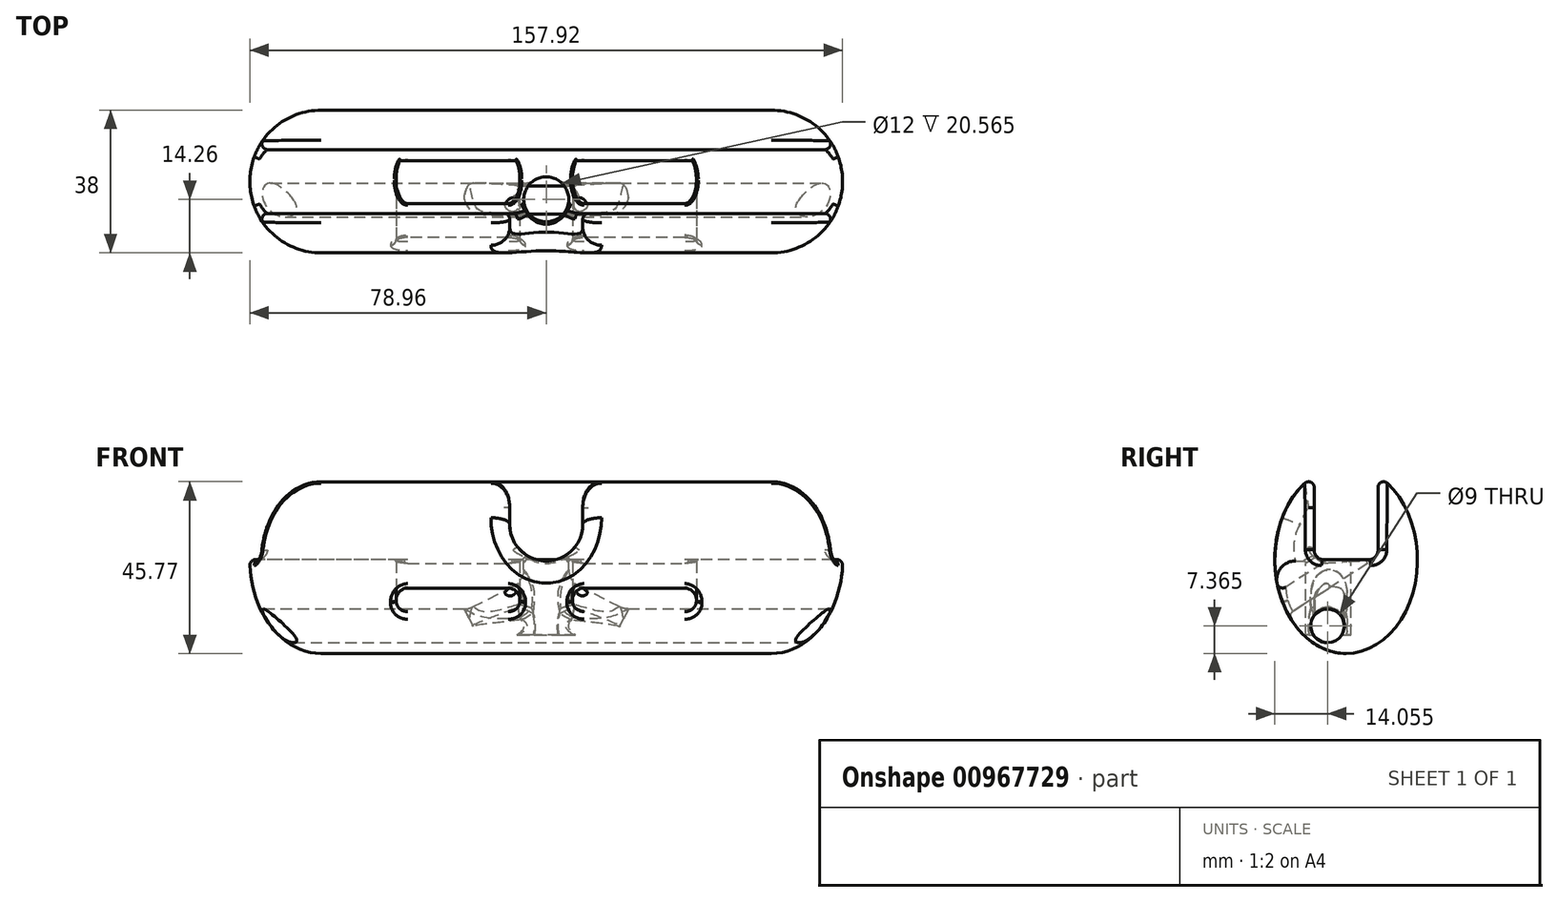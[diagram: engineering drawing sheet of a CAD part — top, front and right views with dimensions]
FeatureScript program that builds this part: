
annotation { "Feature Type Name" : "Feature", "Feature Type Description" : "" }
export const myFeature = defineFeature(function(context is Context, id is Id, definition is map)
    precondition{}
    {
        {
            var Q0;
            Q0=qCreatedBy(makeId("Right.planeOp"),FACE);
            var sketch = newSketch(context, id + "F0", { "sketchPlane" : qUnion([Q0])});
            skEllipse(sketch, "E0", {"center": v(0, 0) * mm, "majorRadius": 25 * mm, "minorRadius": 19 * mm, "majorAxis": v(0, -1)});
            skSolve(sketch);
        }
        {
            var Q0;
            Q0 = qSketchRegion(id + "F0", true);
            extrude(context, id + "F1", {"entities" : qUnion([Q0]), "depth" : 120 * mm, "offsetDistance" : 25 * mm, "symmetric" : true});
        }
        {
            var Q0;
            Q0=makeQuery(id+"F1.opExtrude","CAP_FACE",FACE,{"disambiguationData":[OSD([sQuery(id+"F0.wireOp",EDGE,"E0")])],"isStart":false});
            var sketch = newSketch(context, id + "F2", { "sketchPlane" : qUnion([Q0])});
            skEllipticalArc(sketch, "E1", {});
            skLineSegment(sketch, "E2", {"start": v(0, 25) * mm, "end": v(0, -25) * mm});
            const initialGuessF2  = {"E1": [0, 0, 0, -1, 0.025, 0.019, 3.141592653589793, 0]};
            skSetInitialGuess(sketch, initialGuessF2);
            skSolve(sketch);
        }
        {
            var Q0;
            Q0=makeQuery(id+"F2.imprint","IMPRINT",FACE,{"disambiguationData":[TD([[makeQuery(id+"F2.imprint","IMPRINT",EDGE,{"derivedFrom":sQuery(id+"F2.wireOp",EDGE,"E1")}),1.0]])]});
            var Q1;
            Q1=sQuery(id+"F2.wireOp",EDGE,"E2");
            revolve(context, id + "F3", {"operationType" : NewBodyOperationType.ADD, "surfaceOperationType" : NewSurfaceOperationType.NEW, "entities" : qUnion([Q0]), "axis" : qUnion([Q1]), "revolveType" : RevolveType.FULL});
        }
        {
            var Q0;
            Q0=makeQuery(id+"F1.opExtrude","CAP_FACE",FACE,{"disambiguationData":[OSD([sQuery(id+"F0.wireOp",EDGE,"E0")])],"isStart":true});
            var sketch = newSketch(context, id + "F4", { "sketchPlane" : qUnion([Q0])});
            skEllipticalArc(sketch, "E3", {});
            skLineSegment(sketch, "E4", {"start": v(0, 25) * mm, "end": v(0, -25) * mm});
            const initialGuessF4  = {"E3": [0, 0, 0, -1, 0.025, 0.019, 3.141592653589793, 0]};
            skSetInitialGuess(sketch, initialGuessF4);
            skSolve(sketch);
        }
        {
            var Q0;
            Q0=makeQuery(id+"F4.imprint","IMPRINT",FACE,{"disambiguationData":[TD([[makeQuery(id+"F4.imprint","IMPRINT",EDGE,{"derivedFrom":sQuery(id+"F4.wireOp",EDGE,"E3")}),-1.0]])]});
            var Q1;
            Q1=sQuery(id+"F4.wireOp",EDGE,"E4");
            revolve(context, id + "F5", {"operationType" : NewBodyOperationType.ADD, "surfaceOperationType" : NewSurfaceOperationType.NEW, "entities" : qUnion([Q0]), "axis" : qUnion([Q1]), "revolveType" : RevolveType.FULL});
        }
        {
            var Q0;
            Q0=qCreatedBy(makeId("Right.planeOp"),FACE);
            var sketch = newSketch(context, id + "F6", { "sketchPlane" : qUnion([Q0])});
            skCircle(sketch, "E5", {"center": v(-4.95, -17.63) * mm, "radius": 4.5 * mm});
            skSolve(sketch);
        }
        {
            var Q0;
            Q0 = qSketchRegion(id + "F6", true);
            extrude(context, id + "F7", {"entities" : qUnion([Q0]), "operationType" : NewBodyOperationType.REMOVE, "oppositeDirection" : true, "depth" : 158.8 * mm, "offsetDistance" : 25 * mm, "symmetric" : true});
        }
        {
            var Q0;
            Q0=qCreatedBy(makeId("Top.planeOp"),FACE);
            cPlane(context, id + "F8", {"entities" : qUnion([Q0]), "cplaneType" : CPlaneType.OFFSET, "offset" : 25 * mm, "width" : 150 * mm, "height" : 150 * mm});
        }
        {
            var Q0;
            Q0=qCreatedBy(id+"F8.planeOp",FACE);
            var sketch = newSketch(context, id + "F9", { "sketchPlane" : qUnion([Q0])});
            skLineSegment(sketch, "E6.bottom", {"start": v(79.5, -8.5) * mm, "end": v(-79.5, -8.5) * mm});
            skLineSegment(sketch, "E6.top", {"start": v(79.5, 8.5) * mm, "end": v(-79.5, 8.5) * mm});
            skLineSegment(sketch, "E6.left", {"start": v(79.5, -8.5) * mm, "end": v(79.5, 8.5) * mm});
            skLineSegment(sketch, "E6.right", {"start": v(-79.5, -8.5) * mm, "end": v(-79.5, 8.5) * mm});
            skPoint(sketch, "E6.middle", {"position": v(0, 0) * mm});
            skSolve(sketch);
        }
        {
            var Q0;
            Q0 = qSketchRegion(id + "F9", true);
            extrude(context, id + "F10", {"entities" : qUnion([Q0]), "operationType" : NewBodyOperationType.REMOVE, "oppositeDirection" : true, "depth" : 25 * mm, "offsetDistance" : 25 * mm});
        }
        {
            var Q0;
            Q0=qCreatedBy(makeId("Front.planeOp"),FACE);
            cPlane(context, id + "F11", {"entities" : qUnion([Q0]), "cplaneType" : CPlaneType.OFFSET, "offset" : 5.2 * mm, "width" : 150 * mm, "height" : 150 * mm});
        }
        {
            var Q0;
            Q0=qCreatedBy(id+"F11.planeOp",FACE);
            var sketch = newSketch(context, id + "F12", { "sketchPlane" : qUnion([Q0])});
            skArc(sketch, "E7", {"start": v(-9.74, 9.4) * mm, "mid": v(0, -0.34) * mm, "end": v(9.74, 9.4) * mm});
            skLineSegment(sketch, "E8", {"start": v(-9.74, 9.4) * mm, "end": v(-9.74, 24.15) * mm});
            skLineSegment(sketch, "E9", {"start": v(9.74, 9.4) * mm, "end": v(9.74, 24.15) * mm});
            skLineSegment(sketch, "E10", {"start": v(9.74, 24.15) * mm, "end": v(-9.74, 24.15) * mm});
            skSolve(sketch);
        }
        {
            var Q0;
            Q0 = qSketchRegion(id + "F12", true);
            extrude(context, id + "F13", {"entities" : qUnion([Q0]), "operationType" : NewBodyOperationType.REMOVE, "depth" : 27.5 * mm, "offsetDistance" : 25 * mm});
        }
        {
            var Q0;
            Q0=makeQuery(id+"F13.boolean.opBoolean","INTERSECT",EDGE,{"derivedFrom":[makeQuery(id+"F1.opExtrude","SWEPT_FACE",FACE,{"disambiguationData":[OSD([sQuery(id+"F0.wireOp",EDGE,"E0")])]}),makeQuery(id+"F13.opExtrude","SWEPT_FACE",FACE,{"disambiguationData":[OSD([sQuery(id+"F12.wireOp",EDGE,"E7")])]})]});
            var Q1;
            Q1=makeQuery(id+"F13.boolean.opBoolean","INTERSECT",EDGE,{"derivedFrom":[makeQuery(id+"F1.opExtrude","SWEPT_FACE",FACE,{"disambiguationData":[OSD([sQuery(id+"F0.wireOp",EDGE,"E0")])]}),makeQuery(id+"F13.opExtrude","SWEPT_FACE",FACE,{"disambiguationData":[OSD([sQuery(id+"F12.wireOp",EDGE,"E9")])]})]});
            var Q2;
            Q2=makeQuery(id+"F13.boolean.opBoolean","INTERSECT",EDGE,{"derivedFrom":[makeQuery(id+"F1.opExtrude","SWEPT_FACE",FACE,{"disambiguationData":[OSD([sQuery(id+"F0.wireOp",EDGE,"E0")])]}),makeQuery(id+"F13.opExtrude","SWEPT_FACE",FACE,{"disambiguationData":[OSD([sQuery(id+"F12.wireOp",EDGE,"E8")])]})]});
            fillet(context, id + "F14", {"entities" : qUnion([Q0, Q1, Q2]), "radius" : 5 * mm, "tangentPropagation" : true, "allowEdgeOverflow" : false});
        }
        {
            var Q0;
            {var subQ0=sQuery(id+"F9.wireOp",EDGE,"E6.bottom");Q0=makeQuery(id+"F13.boolean.opBoolean","SPLIT",EDGE,{"disambiguationData":[TD([makeQuery(id+"F3.opRevolve","SWEPT_FACE",FACE,{"disambiguationData":[OSD([sQuery(id+"F2.wireOp",EDGE,"E1")])]})])],"derivedFrom":makeQuery(id+"F10.boolean.opBoolean","COPY",EDGE,{"derivedFrom":makeQuery(id+"F10.opExtrude","CAP_EDGE",EDGE,{"disambiguationData":[OSD([subQ0])],"isStart":false})})});}
            var Q1;
            {var subQ0=sQuery(id+"F9.wireOp",EDGE,"E6.bottom");Q1=makeQuery(id+"F13.boolean.opBoolean","SPLIT",EDGE,{"disambiguationData":[TD([makeQuery(id+"F5.opRevolve","SWEPT_FACE",FACE,{"disambiguationData":[OSD([sQuery(id+"F4.wireOp",EDGE,"E3")])]})])],"derivedFrom":makeQuery(id+"F10.boolean.opBoolean","COPY",EDGE,{"derivedFrom":makeQuery(id+"F10.opExtrude","CAP_EDGE",EDGE,{"disambiguationData":[OSD([subQ0])],"isStart":false})})});}
            var Q2;
            Q2=makeQuery(id+"F10.boolean.opBoolean","COPY",EDGE,{"derivedFrom":makeQuery(id+"F10.opExtrude","CAP_EDGE",EDGE,{"disambiguationData":[OSD([sQuery(id+"F9.wireOp",EDGE,"E6.top")])],"isStart":false})});
            fillet(context, id + "F15", {"entities" : qUnion([Q0, Q1, Q2]), "radius" : 2.5 * mm, "tangentPropagation" : true, "allowEdgeOverflow" : false});
        }
        {
            var Q0;
            Q0=qCreatedBy(makeId("Top.planeOp"),FACE);
            var sketch = newSketch(context, id + "F16", { "sketchPlane" : qUnion([Q0])});
            skCircle(sketch, "E11", {"center": v(0, -4.74) * mm, "radius": 6 * mm});
            skSolve(sketch);
        }
        {
            var Q0;
            {var subQ0=makeQuery(id+"F1.opExtrude","SWEPT_FACE",FACE,{"disambiguationData":[OSD([sQuery(id+"F0.wireOp",EDGE,"E0")])]});var subQ1=makeQuery(id+"F10.opExtrude","SWEPT_FACE",FACE,{"disambiguationData":[OSD([sQuery(id+"F9.wireOp",EDGE,"E6.bottom")])]});Q0=makeQuery(id+"F13.boolean.opBoolean","SPLIT",EDGE,{"disambiguationData":[TD([makeQuery(id+"F5.opRevolve","SWEPT_FACE",FACE,{"disambiguationData":[OSD([sQuery(id+"F4.wireOp",EDGE,"E3")])]})])],"derivedFrom":makeQuery(id+"F10.boolean.opBoolean","INTERSECT",EDGE,{"derivedFrom":[subQ0,subQ1]})});}
            var Q1;
            {var subQ0=makeQuery(id+"F1.opExtrude","SWEPT_FACE",FACE,{"disambiguationData":[OSD([sQuery(id+"F0.wireOp",EDGE,"E0")])]});var subQ1=makeQuery(id+"F10.opExtrude","SWEPT_FACE",FACE,{"disambiguationData":[OSD([sQuery(id+"F9.wireOp",EDGE,"E6.bottom")])]});Q1=makeQuery(id+"F13.boolean.opBoolean","SPLIT",EDGE,{"disambiguationData":[TD([makeQuery(id+"F3.opRevolve","SWEPT_FACE",FACE,{"disambiguationData":[OSD([sQuery(id+"F2.wireOp",EDGE,"E1")])]})])],"derivedFrom":makeQuery(id+"F10.boolean.opBoolean","INTERSECT",EDGE,{"derivedFrom":[subQ0,subQ1]})});}
            fillet(context, id + "F17", {"entities" : qUnion([Q0, Q1]), "radius" : 1.5 * mm, "tangentPropagation" : true, "allowEdgeOverflow" : false});
        }
        {
            var Q0;
            Q0 = qSketchRegion(id + "F16", true);
            extrude(context, id + "F18", {"entities" : qUnion([Q0]), "operationType" : NewBodyOperationType.REMOVE, "oppositeDirection" : true, "depth" : 40.2 * mm, "offsetDistance" : 25 * mm, "symmetric" : true});
        }
        {
            var Q0;
            Q0=makeQuery(id+"F18.boolean.opBoolean","INTERSECT",EDGE,{"derivedFrom":[makeQuery(id+"F10.boolean.opBoolean","COPY",FACE,{"derivedFrom":makeQuery(id+"F10.opExtrude","CAP_FACE",FACE,{"disambiguationData":[OSD([sQuery(id+"F9.wireOp",EDGE,"E6.bottom"),sQuery(id+"F9.wireOp",EDGE,"E6.top"),sQuery(id+"F9.wireOp",EDGE,"E6.left"),sQuery(id+"F9.wireOp",EDGE,"E6.right")])],"isStart":false})}),makeQuery(id+"F18.opExtrude","SWEPT_FACE",FACE,{"disambiguationData":[OSD([sQuery(id+"F16.wireOp",EDGE,"E11")])]})]});
            var Q1;
            {var subQ0=sQuery(id+"F9.wireOp",EDGE,"E6.bottom");Q1=makeQuery(id+"F18.boolean.opBoolean","INTERSECT",EDGE,{"derivedFrom":[makeQuery(id+"F15.opFillet","BLEND_FACE",FACE,{"disambiguationData":[OSD([subQ0]),TDD([makeQuery(id+"F13.boolean.opBoolean","SPLIT",EDGE,{"disambiguationData":[TD([makeQuery(id+"F3.opRevolve","SWEPT_FACE",FACE,{"disambiguationData":[OSD([sQuery(id+"F2.wireOp",EDGE,"E1")])]})])],"derivedFrom":makeQuery(id+"F10.boolean.opBoolean","COPY",EDGE,{"derivedFrom":makeQuery(id+"F10.opExtrude","CAP_EDGE",EDGE,{"disambiguationData":[OSD([subQ0])],"isStart":false})})})])]}),makeQuery(id+"F18.opExtrude","SWEPT_FACE",FACE,{"disambiguationData":[OSD([sQuery(id+"F16.wireOp",EDGE,"E11")])]})]});}
            var Q2;
            {var subQ0=sQuery(id+"F12.wireOp",EDGE,"E7");var subQ1=makeQuery(id+"F13.opExtrude","SWEPT_FACE",FACE,{"disambiguationData":[OSD([subQ0])]});var subQ2=sQuery(id+"F9.wireOp",EDGE,"E6.bottom");Q2=makeQuery(id+"F18.boolean.opBoolean","INTERSECT",EDGE,{"derivedFrom":[makeQuery(id+"F17.opFillet","BLEND_FACE",FACE,{"disambiguationData":[OSD([subQ2,subQ0]),TDD([makeQuery(id+"F15.opFillet","BLEND_EDGE",EDGE,{"blendedFrom":[makeQuery(id+"F13.boolean.opBoolean","SPLIT",EDGE,{"disambiguationData":[TD([makeQuery(id+"F3.opRevolve","SWEPT_FACE",FACE,{"disambiguationData":[OSD([sQuery(id+"F2.wireOp",EDGE,"E1")])]})])],"derivedFrom":makeQuery(id+"F10.boolean.opBoolean","COPY",EDGE,{"derivedFrom":makeQuery(id+"F10.opExtrude","CAP_EDGE",EDGE,{"disambiguationData":[OSD([subQ2])],"isStart":false})})}),makeQuery(id+"F13.boolean.opBoolean","COPY",FACE,{"derivedFrom":subQ1})],"blendedInto":[makeQuery(id+"F13.boolean.opBoolean","COPY",FACE,{"derivedFrom":subQ1})]})])]}),makeQuery(id+"F18.opExtrude","SWEPT_FACE",FACE,{"disambiguationData":[OSD([sQuery(id+"F16.wireOp",EDGE,"E11")])]})]});}
            var Q3;
            Q3=makeQuery(id+"F18.boolean.opBoolean","INTERSECT",EDGE,{"derivedFrom":[makeQuery(id+"F13.boolean.opBoolean","COPY",FACE,{"derivedFrom":makeQuery(id+"F13.opExtrude","SWEPT_FACE",FACE,{"disambiguationData":[OSD([sQuery(id+"F12.wireOp",EDGE,"E7")])]})}),makeQuery(id+"F18.opExtrude","SWEPT_FACE",FACE,{"disambiguationData":[OSD([sQuery(id+"F16.wireOp",EDGE,"E11")])]})]});
            var Q4;
            {var subQ0=sQuery(id+"F12.wireOp",EDGE,"E7");var subQ1=makeQuery(id+"F13.opExtrude","SWEPT_FACE",FACE,{"disambiguationData":[OSD([subQ0])]});var subQ2=sQuery(id+"F9.wireOp",EDGE,"E6.bottom");Q4=makeQuery(id+"F18.boolean.opBoolean","INTERSECT",EDGE,{"derivedFrom":[makeQuery(id+"F17.opFillet","BLEND_FACE",FACE,{"disambiguationData":[OSD([subQ2,subQ0]),TDD([makeQuery(id+"F15.opFillet","BLEND_EDGE",EDGE,{"blendedFrom":[makeQuery(id+"F13.boolean.opBoolean","SPLIT",EDGE,{"disambiguationData":[TD([makeQuery(id+"F5.opRevolve","SWEPT_FACE",FACE,{"disambiguationData":[OSD([sQuery(id+"F4.wireOp",EDGE,"E3")])]})])],"derivedFrom":makeQuery(id+"F10.boolean.opBoolean","COPY",EDGE,{"derivedFrom":makeQuery(id+"F10.opExtrude","CAP_EDGE",EDGE,{"disambiguationData":[OSD([subQ2])],"isStart":false})})}),makeQuery(id+"F13.boolean.opBoolean","COPY",FACE,{"derivedFrom":subQ1})],"blendedInto":[makeQuery(id+"F13.boolean.opBoolean","COPY",FACE,{"derivedFrom":subQ1})]})])]}),makeQuery(id+"F18.opExtrude","SWEPT_FACE",FACE,{"disambiguationData":[OSD([sQuery(id+"F16.wireOp",EDGE,"E11")])]})]});}
            var Q5;
            {var subQ0=sQuery(id+"F9.wireOp",EDGE,"E6.bottom");Q5=makeQuery(id+"F18.boolean.opBoolean","INTERSECT",EDGE,{"derivedFrom":[makeQuery(id+"F15.opFillet","BLEND_FACE",FACE,{"disambiguationData":[OSD([subQ0]),TDD([makeQuery(id+"F13.boolean.opBoolean","SPLIT",EDGE,{"disambiguationData":[TD([makeQuery(id+"F5.opRevolve","SWEPT_FACE",FACE,{"disambiguationData":[OSD([sQuery(id+"F4.wireOp",EDGE,"E3")])]})])],"derivedFrom":makeQuery(id+"F10.boolean.opBoolean","COPY",EDGE,{"derivedFrom":makeQuery(id+"F10.opExtrude","CAP_EDGE",EDGE,{"disambiguationData":[OSD([subQ0])],"isStart":false})})})])]}),makeQuery(id+"F18.opExtrude","SWEPT_FACE",FACE,{"disambiguationData":[OSD([sQuery(id+"F16.wireOp",EDGE,"E11")])]})]});}
            fillet(context, id + "F19", {"entities" : qUnion([Q0, Q1, Q2, Q3, Q4, Q5]), "radius" : 0.65 * mm, "tangentPropagation" : true, "allowEdgeOverflow" : false});
        }
        {
            var Q0;
            Q0=makeQuery(id+"F18.boolean.opBoolean","INTERSECT",EDGE,{"disambiguationData":[OD(0.0)],"derivedFrom":[makeQuery(id+"F7.boolean.opBoolean","COPY",FACE,{"derivedFrom":makeQuery(id+"F7.opExtrude","SWEPT_FACE",FACE,{"disambiguationData":[OSD([sQuery(id+"F6.wireOp",EDGE,"E5")])]})}),makeQuery(id+"F18.opExtrude","SWEPT_FACE",FACE,{"disambiguationData":[OSD([sQuery(id+"F16.wireOp",EDGE,"E11")])]})]});
            var Q1;
            Q1=makeQuery(id+"F18.boolean.opBoolean","INTERSECT",EDGE,{"disambiguationData":[OD(1.0)],"derivedFrom":[makeQuery(id+"F7.boolean.opBoolean","COPY",FACE,{"derivedFrom":makeQuery(id+"F7.opExtrude","SWEPT_FACE",FACE,{"disambiguationData":[OSD([sQuery(id+"F6.wireOp",EDGE,"E5")])]})}),makeQuery(id+"F18.opExtrude","SWEPT_FACE",FACE,{"disambiguationData":[OSD([sQuery(id+"F16.wireOp",EDGE,"E11")])]})]});
            fillet(context, id + "F20", {"entities" : qUnion([Q0, Q1]), "radius" : 5 * mm, "tangentPropagation" : true, "allowEdgeOverflow" : false});
        }
        {
            var Q0;
            Q0=qCreatedBy(makeId("Right.planeOp"),FACE);
            var sketch = newSketch(context, id + "F21", { "sketchPlane" : qUnion([Q0])});
            skLineSegment(sketch, "E12", {"start": v(-25.32, 0) * mm, "end": v(-6.7, -28.91) * mm, "construction": true});
            skSolve(sketch);
        }
        {
            var Q0;
            Q0=qCreatedBy(id+"F11.planeOp",FACE);
            var Q1;
            Q1=sQuery(id+"F21.wireOp",EDGE,"E12");
            cPlane(context, id + "F22", {"entities" : qUnion([Q0, Q1]), "cplaneType" : CPlaneType.LINE_ANGLE, "offset" : 25 * mm, "angle" : 0 * degree, "width" : 150 * mm, "height" : 150 * mm});
        }
        {
            var Q0;
            Q0=qCreatedBy(id+"F22.planeOp",FACE);
            var sketch = newSketch(context, id + "F23", { "sketchPlane" : qUnion([Q0])});
            skLineSegment(sketch, "E13.bottom", {"start": v(40, 2.55) * mm, "end": v(7, 2.55) * mm});
            skLineSegment(sketch, "E13.top", {"start": v(40, -3.95) * mm, "end": v(7, -3.95) * mm});
            skLineSegment(sketch, "E13.left", {"start": v(40, 2.55) * mm, "end": v(40, -3.95) * mm});
            skLineSegment(sketch, "E13.right", {"start": v(7, 2.55) * mm, "end": v(7, -3.95) * mm});
            skLineSegment(sketch, "E14.bottom", {"start": v(-7, 2.55) * mm, "end": v(-40, 2.55) * mm});
            skLineSegment(sketch, "E14.top", {"start": v(-7, -3.95) * mm, "end": v(-40, -3.95) * mm});
            skLineSegment(sketch, "E14.left", {"start": v(-7, 2.55) * mm, "end": v(-7, -3.95) * mm});
            skLineSegment(sketch, "E14.right", {"start": v(-40, 2.55) * mm, "end": v(-40, -3.95) * mm});
            skSolve(sketch);
        }
        {
            var Q0;
            Q0 = qSketchRegion(id + "F23", true);
            extrude(context, id + "F24", {"entities" : qUnion([Q0]), "operationType" : NewBodyOperationType.REMOVE, "depth" : 25.6 * mm, "offsetDistance" : 25 * mm});
        }
        {
            var Q0;
            Q0=makeQuery(id+"F24.boolean.opBoolean","COPY",EDGE,{"derivedFrom":makeQuery(id+"F24.opExtrude","SWEPT_EDGE",EDGE,{"disambiguationData":[OSD([sQuery(id+"F23.wireOp",EDGE,"E13.bottom"),sQuery(id+"F23.wireOp",EDGE,"E13.left")])]})});
            var Q1;
            Q1=makeQuery(id+"F24.boolean.opBoolean","COPY",EDGE,{"derivedFrom":makeQuery(id+"F24.opExtrude","SWEPT_EDGE",EDGE,{"disambiguationData":[OSD([sQuery(id+"F23.wireOp",EDGE,"E13.bottom"),sQuery(id+"F23.wireOp",EDGE,"E13.right")])]})});
            var Q2;
            Q2=makeQuery(id+"F24.boolean.opBoolean","COPY",EDGE,{"derivedFrom":makeQuery(id+"F24.opExtrude","SWEPT_EDGE",EDGE,{"disambiguationData":[OSD([sQuery(id+"F23.wireOp",EDGE,"E14.bottom"),sQuery(id+"F23.wireOp",EDGE,"E14.right")])]})});
            var Q3;
            Q3=makeQuery(id+"F24.boolean.opBoolean","COPY",EDGE,{"derivedFrom":makeQuery(id+"F24.opExtrude","SWEPT_EDGE",EDGE,{"disambiguationData":[OSD([sQuery(id+"F23.wireOp",EDGE,"E14.bottom"),sQuery(id+"F23.wireOp",EDGE,"E14.left")])]})});
            var Q4;
            Q4=makeQuery(id+"F24.boolean.opBoolean","COPY",EDGE,{"derivedFrom":makeQuery(id+"F24.opExtrude","SWEPT_EDGE",EDGE,{"disambiguationData":[OSD([sQuery(id+"F23.wireOp",EDGE,"E13.top"),sQuery(id+"F23.wireOp",EDGE,"E13.left")])]})});
            var Q5;
            Q5=makeQuery(id+"F24.boolean.opBoolean","COPY",EDGE,{"derivedFrom":makeQuery(id+"F24.opExtrude","SWEPT_EDGE",EDGE,{"disambiguationData":[OSD([sQuery(id+"F23.wireOp",EDGE,"E14.top"),sQuery(id+"F23.wireOp",EDGE,"E14.left")])]})});
            var Q6;
            Q6=makeQuery(id+"F24.boolean.opBoolean","COPY",EDGE,{"derivedFrom":makeQuery(id+"F24.opExtrude","SWEPT_EDGE",EDGE,{"disambiguationData":[OSD([sQuery(id+"F23.wireOp",EDGE,"E14.top"),sQuery(id+"F23.wireOp",EDGE,"E14.right")])]})});
            var Q7;
            Q7=makeQuery(id+"F24.boolean.opBoolean","COPY",EDGE,{"derivedFrom":makeQuery(id+"F24.opExtrude","SWEPT_EDGE",EDGE,{"disambiguationData":[OSD([sQuery(id+"F23.wireOp",EDGE,"E13.top"),sQuery(id+"F23.wireOp",EDGE,"E13.right")])]})});
            fillet(context, id + "F25", {"entities" : qUnion([Q0, Q1, Q2, Q3, Q4, Q5, Q6, Q7]), "radius" : 3.14 * mm, "tangentPropagation" : true, "allowEdgeOverflow" : false});
        }
        {
            var Q0;
            Q0=makeQuery(id+"F24.boolean.opBoolean","INTERSECT",EDGE,{"derivedFrom":[makeQuery(id+"F1.opExtrude","SWEPT_FACE",FACE,{"disambiguationData":[OSD([sQuery(id+"F0.wireOp",EDGE,"E0")])]}),makeQuery(id+"F24.opExtrude","SWEPT_FACE",FACE,{"disambiguationData":[OSD([sQuery(id+"F23.wireOp",EDGE,"E13.bottom")])]})]});
            var Q1;
            Q1=makeQuery(id+"F25.opFillet","BLEND_EDGE",EDGE,{"blendedFrom":[makeQuery(id+"F24.boolean.opBoolean","COPY",EDGE,{"derivedFrom":makeQuery(id+"F24.opExtrude","SWEPT_EDGE",EDGE,{"disambiguationData":[OSD([sQuery(id+"F23.wireOp",EDGE,"E13.bottom"),sQuery(id+"F23.wireOp",EDGE,"E13.left")])]})}),makeQuery(id+"F1.opExtrude","SWEPT_FACE",FACE,{"disambiguationData":[OSD([sQuery(id+"F0.wireOp",EDGE,"E0")])]})],"blendedInto":[makeQuery(id+"F1.opExtrude","SWEPT_FACE",FACE,{"disambiguationData":[OSD([sQuery(id+"F0.wireOp",EDGE,"E0")])]})]});
            var Q2;
            Q2=makeQuery(id+"F25.opFillet","BLEND_EDGE",EDGE,{"blendedFrom":[makeQuery(id+"F24.boolean.opBoolean","COPY",EDGE,{"derivedFrom":makeQuery(id+"F24.opExtrude","SWEPT_EDGE",EDGE,{"disambiguationData":[OSD([sQuery(id+"F23.wireOp",EDGE,"E13.top"),sQuery(id+"F23.wireOp",EDGE,"E13.left")])]})}),makeQuery(id+"F1.opExtrude","SWEPT_FACE",FACE,{"disambiguationData":[OSD([sQuery(id+"F0.wireOp",EDGE,"E0")])]})],"blendedInto":[makeQuery(id+"F1.opExtrude","SWEPT_FACE",FACE,{"disambiguationData":[OSD([sQuery(id+"F0.wireOp",EDGE,"E0")])]})]});
            var Q3;
            Q3=makeQuery(id+"F24.boolean.opBoolean","INTERSECT",EDGE,{"derivedFrom":[makeQuery(id+"F1.opExtrude","SWEPT_FACE",FACE,{"disambiguationData":[OSD([sQuery(id+"F0.wireOp",EDGE,"E0")])]}),makeQuery(id+"F24.opExtrude","SWEPT_FACE",FACE,{"disambiguationData":[OSD([sQuery(id+"F23.wireOp",EDGE,"E13.top")])]})]});
            var Q4;
            Q4=makeQuery(id+"F25.opFillet","BLEND_EDGE",EDGE,{"blendedFrom":[makeQuery(id+"F24.boolean.opBoolean","COPY",EDGE,{"derivedFrom":makeQuery(id+"F24.opExtrude","SWEPT_EDGE",EDGE,{"disambiguationData":[OSD([sQuery(id+"F23.wireOp",EDGE,"E13.top"),sQuery(id+"F23.wireOp",EDGE,"E13.right")])]})}),makeQuery(id+"F1.opExtrude","SWEPT_FACE",FACE,{"disambiguationData":[OSD([sQuery(id+"F0.wireOp",EDGE,"E0")])]})],"blendedInto":[makeQuery(id+"F1.opExtrude","SWEPT_FACE",FACE,{"disambiguationData":[OSD([sQuery(id+"F0.wireOp",EDGE,"E0")])]})]});
            var Q5;
            Q5=makeQuery(id+"F25.opFillet","BLEND_EDGE",EDGE,{"blendedFrom":[makeQuery(id+"F24.boolean.opBoolean","COPY",EDGE,{"derivedFrom":makeQuery(id+"F24.opExtrude","SWEPT_EDGE",EDGE,{"disambiguationData":[OSD([sQuery(id+"F23.wireOp",EDGE,"E13.bottom"),sQuery(id+"F23.wireOp",EDGE,"E13.right")])]})}),makeQuery(id+"F1.opExtrude","SWEPT_FACE",FACE,{"disambiguationData":[OSD([sQuery(id+"F0.wireOp",EDGE,"E0")])]})],"blendedInto":[makeQuery(id+"F1.opExtrude","SWEPT_FACE",FACE,{"disambiguationData":[OSD([sQuery(id+"F0.wireOp",EDGE,"E0")])]})]});
            var Q6;
            Q6=makeQuery(id+"F24.boolean.opBoolean","INTERSECT",EDGE,{"derivedFrom":[makeQuery(id+"F1.opExtrude","SWEPT_FACE",FACE,{"disambiguationData":[OSD([sQuery(id+"F0.wireOp",EDGE,"E0")])]}),makeQuery(id+"F24.opExtrude","SWEPT_FACE",FACE,{"disambiguationData":[OSD([sQuery(id+"F23.wireOp",EDGE,"E13.right")])]})]});
            var Q7;
            Q7=makeQuery(id+"F24.boolean.opBoolean","INTERSECT",EDGE,{"derivedFrom":[makeQuery(id+"F1.opExtrude","SWEPT_FACE",FACE,{"disambiguationData":[OSD([sQuery(id+"F0.wireOp",EDGE,"E0")])]}),makeQuery(id+"F24.opExtrude","SWEPT_FACE",FACE,{"disambiguationData":[OSD([sQuery(id+"F23.wireOp",EDGE,"E13.left")])]})]});
            var Q8;
            Q8=makeQuery(id+"F25.opFillet","BLEND_EDGE",EDGE,{"blendedFrom":[makeQuery(id+"F24.boolean.opBoolean","COPY",EDGE,{"derivedFrom":makeQuery(id+"F24.opExtrude","SWEPT_EDGE",EDGE,{"disambiguationData":[OSD([sQuery(id+"F23.wireOp",EDGE,"E14.top"),sQuery(id+"F23.wireOp",EDGE,"E14.right")])]})}),makeQuery(id+"F1.opExtrude","SWEPT_FACE",FACE,{"disambiguationData":[OSD([sQuery(id+"F0.wireOp",EDGE,"E0")])]})],"blendedInto":[makeQuery(id+"F1.opExtrude","SWEPT_FACE",FACE,{"disambiguationData":[OSD([sQuery(id+"F0.wireOp",EDGE,"E0")])]})]});
            var Q9;
            Q9=makeQuery(id+"F24.boolean.opBoolean","INTERSECT",EDGE,{"derivedFrom":[makeQuery(id+"F1.opExtrude","SWEPT_FACE",FACE,{"disambiguationData":[OSD([sQuery(id+"F0.wireOp",EDGE,"E0")])]}),makeQuery(id+"F24.opExtrude","SWEPT_FACE",FACE,{"disambiguationData":[OSD([sQuery(id+"F23.wireOp",EDGE,"E14.right")])]})]});
            var Q10;
            Q10=makeQuery(id+"F25.opFillet","BLEND_EDGE",EDGE,{"blendedFrom":[makeQuery(id+"F24.boolean.opBoolean","COPY",EDGE,{"derivedFrom":makeQuery(id+"F24.opExtrude","SWEPT_EDGE",EDGE,{"disambiguationData":[OSD([sQuery(id+"F23.wireOp",EDGE,"E14.bottom"),sQuery(id+"F23.wireOp",EDGE,"E14.right")])]})}),makeQuery(id+"F1.opExtrude","SWEPT_FACE",FACE,{"disambiguationData":[OSD([sQuery(id+"F0.wireOp",EDGE,"E0")])]})],"blendedInto":[makeQuery(id+"F1.opExtrude","SWEPT_FACE",FACE,{"disambiguationData":[OSD([sQuery(id+"F0.wireOp",EDGE,"E0")])]})]});
            var Q11;
            Q11=makeQuery(id+"F24.boolean.opBoolean","INTERSECT",EDGE,{"derivedFrom":[makeQuery(id+"F1.opExtrude","SWEPT_FACE",FACE,{"disambiguationData":[OSD([sQuery(id+"F0.wireOp",EDGE,"E0")])]}),makeQuery(id+"F24.opExtrude","SWEPT_FACE",FACE,{"disambiguationData":[OSD([sQuery(id+"F23.wireOp",EDGE,"E14.bottom")])]})]});
            var Q12;
            Q12=makeQuery(id+"F24.boolean.opBoolean","INTERSECT",EDGE,{"derivedFrom":[makeQuery(id+"F1.opExtrude","SWEPT_FACE",FACE,{"disambiguationData":[OSD([sQuery(id+"F0.wireOp",EDGE,"E0")])]}),makeQuery(id+"F24.opExtrude","SWEPT_FACE",FACE,{"disambiguationData":[OSD([sQuery(id+"F23.wireOp",EDGE,"E14.top")])]})]});
            var Q13;
            Q13=makeQuery(id+"F25.opFillet","BLEND_EDGE",EDGE,{"blendedFrom":[makeQuery(id+"F24.boolean.opBoolean","COPY",EDGE,{"derivedFrom":makeQuery(id+"F24.opExtrude","SWEPT_EDGE",EDGE,{"disambiguationData":[OSD([sQuery(id+"F23.wireOp",EDGE,"E14.bottom"),sQuery(id+"F23.wireOp",EDGE,"E14.left")])]})}),makeQuery(id+"F1.opExtrude","SWEPT_FACE",FACE,{"disambiguationData":[OSD([sQuery(id+"F0.wireOp",EDGE,"E0")])]})],"blendedInto":[makeQuery(id+"F1.opExtrude","SWEPT_FACE",FACE,{"disambiguationData":[OSD([sQuery(id+"F0.wireOp",EDGE,"E0")])]})]});
            var Q14;
            Q14=makeQuery(id+"F25.opFillet","BLEND_EDGE",EDGE,{"blendedFrom":[makeQuery(id+"F24.boolean.opBoolean","COPY",EDGE,{"derivedFrom":makeQuery(id+"F24.opExtrude","SWEPT_EDGE",EDGE,{"disambiguationData":[OSD([sQuery(id+"F23.wireOp",EDGE,"E14.top"),sQuery(id+"F23.wireOp",EDGE,"E14.left")])]})}),makeQuery(id+"F1.opExtrude","SWEPT_FACE",FACE,{"disambiguationData":[OSD([sQuery(id+"F0.wireOp",EDGE,"E0")])]})],"blendedInto":[makeQuery(id+"F1.opExtrude","SWEPT_FACE",FACE,{"disambiguationData":[OSD([sQuery(id+"F0.wireOp",EDGE,"E0")])]})]});
            var Q15;
            Q15=makeQuery(id+"F24.boolean.opBoolean","INTERSECT",EDGE,{"derivedFrom":[makeQuery(id+"F1.opExtrude","SWEPT_FACE",FACE,{"disambiguationData":[OSD([sQuery(id+"F0.wireOp",EDGE,"E0")])]}),makeQuery(id+"F24.opExtrude","SWEPT_FACE",FACE,{"disambiguationData":[OSD([sQuery(id+"F23.wireOp",EDGE,"E14.left")])]})]});
            fillet(context, id + "F26", {"entities" : qUnion([Q0, Q1, Q2, Q3, Q4, Q5, Q6, Q7, Q8, Q9, Q10, Q11, Q12, Q13, Q14, Q15]), "radius" : 1.5 * mm, "tangentPropagation" : true, "allowEdgeOverflow" : false});
        }
        {
            var Q0;
            Q0=makeQuery(id+"F24.boolean.opBoolean","INTERSECT",EDGE,{"derivedFrom":[makeQuery(id+"F10.boolean.opBoolean","COPY",FACE,{"derivedFrom":makeQuery(id+"F10.opExtrude","CAP_FACE",FACE,{"disambiguationData":[OSD([sQuery(id+"F9.wireOp",EDGE,"E6.bottom"),sQuery(id+"F9.wireOp",EDGE,"E6.top"),sQuery(id+"F9.wireOp",EDGE,"E6.left"),sQuery(id+"F9.wireOp",EDGE,"E6.right")])],"isStart":false})}),makeQuery(id+"F24.opExtrude","SWEPT_FACE",FACE,{"disambiguationData":[OSD([sQuery(id+"F23.wireOp",EDGE,"E14.bottom")])]})]});
            var Q1;
            Q1=makeQuery(id+"F24.boolean.opBoolean","INTERSECT",EDGE,{"derivedFrom":[makeQuery(id+"F10.boolean.opBoolean","COPY",FACE,{"derivedFrom":makeQuery(id+"F10.opExtrude","CAP_FACE",FACE,{"disambiguationData":[OSD([sQuery(id+"F9.wireOp",EDGE,"E6.bottom"),sQuery(id+"F9.wireOp",EDGE,"E6.top"),sQuery(id+"F9.wireOp",EDGE,"E6.left"),sQuery(id+"F9.wireOp",EDGE,"E6.right")])],"isStart":false})}),makeQuery(id+"F24.opExtrude","CAP_FACE",FACE,{"disambiguationData":[OSD([sQuery(id+"F23.wireOp",EDGE,"E14.bottom"),sQuery(id+"F23.wireOp",EDGE,"E14.top"),sQuery(id+"F23.wireOp",EDGE,"E14.left"),sQuery(id+"F23.wireOp",EDGE,"E14.right")])],"isStart":false})]});
            var Q2;
            Q2=makeQuery(id+"F25.opFillet","BLEND_EDGE",EDGE,{"blendedFrom":[makeQuery(id+"F24.boolean.opBoolean","COPY",EDGE,{"derivedFrom":makeQuery(id+"F24.opExtrude","SWEPT_EDGE",EDGE,{"disambiguationData":[OSD([sQuery(id+"F23.wireOp",EDGE,"E14.top"),sQuery(id+"F23.wireOp",EDGE,"E14.left")])]})}),makeQuery(id+"F10.boolean.opBoolean","COPY",FACE,{"derivedFrom":makeQuery(id+"F10.opExtrude","CAP_FACE",FACE,{"disambiguationData":[OSD([sQuery(id+"F9.wireOp",EDGE,"E6.bottom"),sQuery(id+"F9.wireOp",EDGE,"E6.top"),sQuery(id+"F9.wireOp",EDGE,"E6.left"),sQuery(id+"F9.wireOp",EDGE,"E6.right")])],"isStart":false})})],"blendedInto":[makeQuery(id+"F10.boolean.opBoolean","COPY",FACE,{"derivedFrom":makeQuery(id+"F10.opExtrude","CAP_FACE",FACE,{"disambiguationData":[OSD([sQuery(id+"F9.wireOp",EDGE,"E6.bottom"),sQuery(id+"F9.wireOp",EDGE,"E6.top"),sQuery(id+"F9.wireOp",EDGE,"E6.left"),sQuery(id+"F9.wireOp",EDGE,"E6.right")])],"isStart":false})})]});
            var Q3;
            Q3=makeQuery(id+"F25.opFillet","BLEND_EDGE",EDGE,{"blendedFrom":[makeQuery(id+"F24.boolean.opBoolean","COPY",EDGE,{"derivedFrom":makeQuery(id+"F24.opExtrude","SWEPT_EDGE",EDGE,{"disambiguationData":[OSD([sQuery(id+"F23.wireOp",EDGE,"E14.bottom"),sQuery(id+"F23.wireOp",EDGE,"E14.left")])]})}),makeQuery(id+"F10.boolean.opBoolean","COPY",FACE,{"derivedFrom":makeQuery(id+"F10.opExtrude","CAP_FACE",FACE,{"disambiguationData":[OSD([sQuery(id+"F9.wireOp",EDGE,"E6.bottom"),sQuery(id+"F9.wireOp",EDGE,"E6.top"),sQuery(id+"F9.wireOp",EDGE,"E6.left"),sQuery(id+"F9.wireOp",EDGE,"E6.right")])],"isStart":false})})],"blendedInto":[makeQuery(id+"F10.boolean.opBoolean","COPY",FACE,{"derivedFrom":makeQuery(id+"F10.opExtrude","CAP_FACE",FACE,{"disambiguationData":[OSD([sQuery(id+"F9.wireOp",EDGE,"E6.bottom"),sQuery(id+"F9.wireOp",EDGE,"E6.top"),sQuery(id+"F9.wireOp",EDGE,"E6.left"),sQuery(id+"F9.wireOp",EDGE,"E6.right")])],"isStart":false})})]});
            var Q4;
            Q4=makeQuery(id+"F24.boolean.opBoolean","INTERSECT",EDGE,{"derivedFrom":[makeQuery(id+"F10.boolean.opBoolean","COPY",FACE,{"derivedFrom":makeQuery(id+"F10.opExtrude","CAP_FACE",FACE,{"disambiguationData":[OSD([sQuery(id+"F9.wireOp",EDGE,"E6.bottom"),sQuery(id+"F9.wireOp",EDGE,"E6.top"),sQuery(id+"F9.wireOp",EDGE,"E6.left"),sQuery(id+"F9.wireOp",EDGE,"E6.right")])],"isStart":false})}),makeQuery(id+"F24.opExtrude","SWEPT_FACE",FACE,{"disambiguationData":[OSD([sQuery(id+"F23.wireOp",EDGE,"E14.left")])]})]});
            var Q5;
            Q5=makeQuery(id+"F25.opFillet","BLEND_EDGE",EDGE,{"blendedFrom":[makeQuery(id+"F24.boolean.opBoolean","COPY",EDGE,{"derivedFrom":makeQuery(id+"F24.opExtrude","SWEPT_EDGE",EDGE,{"disambiguationData":[OSD([sQuery(id+"F23.wireOp",EDGE,"E14.bottom"),sQuery(id+"F23.wireOp",EDGE,"E14.right")])]})}),makeQuery(id+"F10.boolean.opBoolean","COPY",FACE,{"derivedFrom":makeQuery(id+"F10.opExtrude","CAP_FACE",FACE,{"disambiguationData":[OSD([sQuery(id+"F9.wireOp",EDGE,"E6.bottom"),sQuery(id+"F9.wireOp",EDGE,"E6.top"),sQuery(id+"F9.wireOp",EDGE,"E6.left"),sQuery(id+"F9.wireOp",EDGE,"E6.right")])],"isStart":false})})],"blendedInto":[makeQuery(id+"F10.boolean.opBoolean","COPY",FACE,{"derivedFrom":makeQuery(id+"F10.opExtrude","CAP_FACE",FACE,{"disambiguationData":[OSD([sQuery(id+"F9.wireOp",EDGE,"E6.bottom"),sQuery(id+"F9.wireOp",EDGE,"E6.top"),sQuery(id+"F9.wireOp",EDGE,"E6.left"),sQuery(id+"F9.wireOp",EDGE,"E6.right")])],"isStart":false})})]});
            var Q6;
            Q6=makeQuery(id+"F25.opFillet","BLEND_EDGE",EDGE,{"blendedFrom":[makeQuery(id+"F24.boolean.opBoolean","COPY",EDGE,{"derivedFrom":makeQuery(id+"F24.opExtrude","SWEPT_EDGE",EDGE,{"disambiguationData":[OSD([sQuery(id+"F23.wireOp",EDGE,"E14.top"),sQuery(id+"F23.wireOp",EDGE,"E14.right")])]})}),makeQuery(id+"F10.boolean.opBoolean","COPY",FACE,{"derivedFrom":makeQuery(id+"F10.opExtrude","CAP_FACE",FACE,{"disambiguationData":[OSD([sQuery(id+"F9.wireOp",EDGE,"E6.bottom"),sQuery(id+"F9.wireOp",EDGE,"E6.top"),sQuery(id+"F9.wireOp",EDGE,"E6.left"),sQuery(id+"F9.wireOp",EDGE,"E6.right")])],"isStart":false})})],"blendedInto":[makeQuery(id+"F10.boolean.opBoolean","COPY",FACE,{"derivedFrom":makeQuery(id+"F10.opExtrude","CAP_FACE",FACE,{"disambiguationData":[OSD([sQuery(id+"F9.wireOp",EDGE,"E6.bottom"),sQuery(id+"F9.wireOp",EDGE,"E6.top"),sQuery(id+"F9.wireOp",EDGE,"E6.left"),sQuery(id+"F9.wireOp",EDGE,"E6.right")])],"isStart":false})})]});
            var Q7;
            Q7=makeQuery(id+"F24.boolean.opBoolean","INTERSECT",EDGE,{"derivedFrom":[makeQuery(id+"F10.boolean.opBoolean","COPY",FACE,{"derivedFrom":makeQuery(id+"F10.opExtrude","CAP_FACE",FACE,{"disambiguationData":[OSD([sQuery(id+"F9.wireOp",EDGE,"E6.bottom"),sQuery(id+"F9.wireOp",EDGE,"E6.top"),sQuery(id+"F9.wireOp",EDGE,"E6.left"),sQuery(id+"F9.wireOp",EDGE,"E6.right")])],"isStart":false})}),makeQuery(id+"F24.opExtrude","SWEPT_FACE",FACE,{"disambiguationData":[OSD([sQuery(id+"F23.wireOp",EDGE,"E14.right")])]})]});
            var Q8;
            Q8=makeQuery(id+"F25.opFillet","BLEND_EDGE",EDGE,{"blendedFrom":[makeQuery(id+"F24.boolean.opBoolean","COPY",EDGE,{"derivedFrom":makeQuery(id+"F24.opExtrude","SWEPT_EDGE",EDGE,{"disambiguationData":[OSD([sQuery(id+"F23.wireOp",EDGE,"E13.bottom"),sQuery(id+"F23.wireOp",EDGE,"E13.right")])]})}),makeQuery(id+"F10.boolean.opBoolean","COPY",FACE,{"derivedFrom":makeQuery(id+"F10.opExtrude","CAP_FACE",FACE,{"disambiguationData":[OSD([sQuery(id+"F9.wireOp",EDGE,"E6.bottom"),sQuery(id+"F9.wireOp",EDGE,"E6.top"),sQuery(id+"F9.wireOp",EDGE,"E6.left"),sQuery(id+"F9.wireOp",EDGE,"E6.right")])],"isStart":false})})],"blendedInto":[makeQuery(id+"F10.boolean.opBoolean","COPY",FACE,{"derivedFrom":makeQuery(id+"F10.opExtrude","CAP_FACE",FACE,{"disambiguationData":[OSD([sQuery(id+"F9.wireOp",EDGE,"E6.bottom"),sQuery(id+"F9.wireOp",EDGE,"E6.top"),sQuery(id+"F9.wireOp",EDGE,"E6.left"),sQuery(id+"F9.wireOp",EDGE,"E6.right")])],"isStart":false})})]});
            var Q9;
            Q9=makeQuery(id+"F25.opFillet","BLEND_EDGE",EDGE,{"blendedFrom":[makeQuery(id+"F24.boolean.opBoolean","COPY",EDGE,{"derivedFrom":makeQuery(id+"F24.opExtrude","SWEPT_EDGE",EDGE,{"disambiguationData":[OSD([sQuery(id+"F23.wireOp",EDGE,"E13.top"),sQuery(id+"F23.wireOp",EDGE,"E13.right")])]})}),makeQuery(id+"F10.boolean.opBoolean","COPY",FACE,{"derivedFrom":makeQuery(id+"F10.opExtrude","CAP_FACE",FACE,{"disambiguationData":[OSD([sQuery(id+"F9.wireOp",EDGE,"E6.bottom"),sQuery(id+"F9.wireOp",EDGE,"E6.top"),sQuery(id+"F9.wireOp",EDGE,"E6.left"),sQuery(id+"F9.wireOp",EDGE,"E6.right")])],"isStart":false})})],"blendedInto":[makeQuery(id+"F10.boolean.opBoolean","COPY",FACE,{"derivedFrom":makeQuery(id+"F10.opExtrude","CAP_FACE",FACE,{"disambiguationData":[OSD([sQuery(id+"F9.wireOp",EDGE,"E6.bottom"),sQuery(id+"F9.wireOp",EDGE,"E6.top"),sQuery(id+"F9.wireOp",EDGE,"E6.left"),sQuery(id+"F9.wireOp",EDGE,"E6.right")])],"isStart":false})})]});
            var Q10;
            Q10=makeQuery(id+"F24.boolean.opBoolean","INTERSECT",EDGE,{"derivedFrom":[makeQuery(id+"F10.boolean.opBoolean","COPY",FACE,{"derivedFrom":makeQuery(id+"F10.opExtrude","CAP_FACE",FACE,{"disambiguationData":[OSD([sQuery(id+"F9.wireOp",EDGE,"E6.bottom"),sQuery(id+"F9.wireOp",EDGE,"E6.top"),sQuery(id+"F9.wireOp",EDGE,"E6.left"),sQuery(id+"F9.wireOp",EDGE,"E6.right")])],"isStart":false})}),makeQuery(id+"F24.opExtrude","SWEPT_FACE",FACE,{"disambiguationData":[OSD([sQuery(id+"F23.wireOp",EDGE,"E13.right")])]})]});
            var Q11;
            Q11=makeQuery(id+"F24.boolean.opBoolean","INTERSECT",EDGE,{"derivedFrom":[makeQuery(id+"F10.boolean.opBoolean","COPY",FACE,{"derivedFrom":makeQuery(id+"F10.opExtrude","CAP_FACE",FACE,{"disambiguationData":[OSD([sQuery(id+"F9.wireOp",EDGE,"E6.bottom"),sQuery(id+"F9.wireOp",EDGE,"E6.top"),sQuery(id+"F9.wireOp",EDGE,"E6.left"),sQuery(id+"F9.wireOp",EDGE,"E6.right")])],"isStart":false})}),makeQuery(id+"F24.opExtrude","CAP_FACE",FACE,{"disambiguationData":[OSD([sQuery(id+"F23.wireOp",EDGE,"E13.bottom"),sQuery(id+"F23.wireOp",EDGE,"E13.top"),sQuery(id+"F23.wireOp",EDGE,"E13.left"),sQuery(id+"F23.wireOp",EDGE,"E13.right")])],"isStart":false})]});
            var Q12;
            Q12=makeQuery(id+"F24.boolean.opBoolean","INTERSECT",EDGE,{"derivedFrom":[makeQuery(id+"F10.boolean.opBoolean","COPY",FACE,{"derivedFrom":makeQuery(id+"F10.opExtrude","CAP_FACE",FACE,{"disambiguationData":[OSD([sQuery(id+"F9.wireOp",EDGE,"E6.bottom"),sQuery(id+"F9.wireOp",EDGE,"E6.top"),sQuery(id+"F9.wireOp",EDGE,"E6.left"),sQuery(id+"F9.wireOp",EDGE,"E6.right")])],"isStart":false})}),makeQuery(id+"F24.opExtrude","SWEPT_FACE",FACE,{"disambiguationData":[OSD([sQuery(id+"F23.wireOp",EDGE,"E13.bottom")])]})]});
            var Q13;
            Q13=makeQuery(id+"F25.opFillet","BLEND_EDGE",EDGE,{"blendedFrom":[makeQuery(id+"F24.boolean.opBoolean","COPY",EDGE,{"derivedFrom":makeQuery(id+"F24.opExtrude","SWEPT_EDGE",EDGE,{"disambiguationData":[OSD([sQuery(id+"F23.wireOp",EDGE,"E13.top"),sQuery(id+"F23.wireOp",EDGE,"E13.left")])]})}),makeQuery(id+"F10.boolean.opBoolean","COPY",FACE,{"derivedFrom":makeQuery(id+"F10.opExtrude","CAP_FACE",FACE,{"disambiguationData":[OSD([sQuery(id+"F9.wireOp",EDGE,"E6.bottom"),sQuery(id+"F9.wireOp",EDGE,"E6.top"),sQuery(id+"F9.wireOp",EDGE,"E6.left"),sQuery(id+"F9.wireOp",EDGE,"E6.right")])],"isStart":false})})],"blendedInto":[makeQuery(id+"F10.boolean.opBoolean","COPY",FACE,{"derivedFrom":makeQuery(id+"F10.opExtrude","CAP_FACE",FACE,{"disambiguationData":[OSD([sQuery(id+"F9.wireOp",EDGE,"E6.bottom"),sQuery(id+"F9.wireOp",EDGE,"E6.top"),sQuery(id+"F9.wireOp",EDGE,"E6.left"),sQuery(id+"F9.wireOp",EDGE,"E6.right")])],"isStart":false})})]});
            var Q14;
            Q14=makeQuery(id+"F25.opFillet","BLEND_EDGE",EDGE,{"blendedFrom":[makeQuery(id+"F24.boolean.opBoolean","COPY",EDGE,{"derivedFrom":makeQuery(id+"F24.opExtrude","SWEPT_EDGE",EDGE,{"disambiguationData":[OSD([sQuery(id+"F23.wireOp",EDGE,"E13.bottom"),sQuery(id+"F23.wireOp",EDGE,"E13.left")])]})}),makeQuery(id+"F10.boolean.opBoolean","COPY",FACE,{"derivedFrom":makeQuery(id+"F10.opExtrude","CAP_FACE",FACE,{"disambiguationData":[OSD([sQuery(id+"F9.wireOp",EDGE,"E6.bottom"),sQuery(id+"F9.wireOp",EDGE,"E6.top"),sQuery(id+"F9.wireOp",EDGE,"E6.left"),sQuery(id+"F9.wireOp",EDGE,"E6.right")])],"isStart":false})})],"blendedInto":[makeQuery(id+"F10.boolean.opBoolean","COPY",FACE,{"derivedFrom":makeQuery(id+"F10.opExtrude","CAP_FACE",FACE,{"disambiguationData":[OSD([sQuery(id+"F9.wireOp",EDGE,"E6.bottom"),sQuery(id+"F9.wireOp",EDGE,"E6.top"),sQuery(id+"F9.wireOp",EDGE,"E6.left"),sQuery(id+"F9.wireOp",EDGE,"E6.right")])],"isStart":false})})]});
            var Q15;
            Q15=makeQuery(id+"F24.boolean.opBoolean","INTERSECT",EDGE,{"derivedFrom":[makeQuery(id+"F10.boolean.opBoolean","COPY",FACE,{"derivedFrom":makeQuery(id+"F10.opExtrude","CAP_FACE",FACE,{"disambiguationData":[OSD([sQuery(id+"F9.wireOp",EDGE,"E6.bottom"),sQuery(id+"F9.wireOp",EDGE,"E6.top"),sQuery(id+"F9.wireOp",EDGE,"E6.left"),sQuery(id+"F9.wireOp",EDGE,"E6.right")])],"isStart":false})}),makeQuery(id+"F24.opExtrude","SWEPT_FACE",FACE,{"disambiguationData":[OSD([sQuery(id+"F23.wireOp",EDGE,"E13.left")])]})]});
            fillet(context, id + "F27", {"entities" : qUnion([Q0, Q1, Q2, Q3, Q4, Q5, Q6, Q7, Q8, Q9, Q10, Q11, Q12, Q13, Q14, Q15]), "radius" : .5 * mm, "tangentPropagation" : true, "allowEdgeOverflow" : false});
        }
        {
            var Q0;
            Q0=qCreatedBy(makeId("Front.planeOp"),FACE);
            var sketch = newSketch(context, id + "F28", { "sketchPlane" : qUnion([Q0])});
            skLineSegment(sketch, "E15", {"start": v(0, 0) * mm, "end": v(0, 39.93) * mm, "construction": true});
            skSolve(sketch);
        }
        {
            var Q0;
            Q0=qCreatedBy(makeId("Front.planeOp"),FACE);
            var sketch = newSketch(context, id + "F29", { "sketchPlane" : qUnion([Q0])});
            skLineSegment(sketch, "E16", {"start": v(-6.76, 13.51) * mm, "end": v(7.79, -15.2) * mm, "construction": true});
            skSolve(sketch);
        }
        {
            var Q0;
            Q0=qCreatedBy(makeId("Right.planeOp"),FACE);
            var Q1;
            Q1=sQuery(id+"F29.wireOp",EDGE,"E16");
            cPlane(context, id + "F30", {"entities" : qUnion([Q0, Q1]), "cplaneType" : CPlaneType.LINE_ANGLE, "offset" : 25 * mm, "angle" : 0 * degree, "width" : 150 * mm, "height" : 150 * mm});
        }
        {
            var Q0;
            Q0=qCreatedBy(makeId("Right.planeOp"),FACE);
            var sketch = newSketch(context, id + "F31", { "sketchPlane" : qUnion([Q0])});
            skLineSegment(sketch, "E17", {"start": v(0, 0) * mm, "end": v(-21.55, 0) * mm, "construction": true});
            skSolve(sketch);
        }
        {
            var Q0;
            Q0=qCreatedBy(id+"F30.planeOp",FACE);
            var sketch = newSketch(context, id + "F32", { "sketchPlane" : qUnion([Q0])});
            skCircle(sketch, "E18", {"center": v(4.42, -6.39) * mm, "radius": 4 * mm});
            skSolve(sketch);
        }
        {
            var Q0;
            Q0 = qSketchRegion(id + "F32", true);
            extrude(context, id + "F33", {"entities" : qUnion([Q0]), "operationType" : NewBodyOperationType.REMOVE, "depth" : 25.5 * mm, "offsetDistance" : 25 * mm});
        }
        {
            var Q0;
            Q0=qCreatedBy(makeId("Front.planeOp"),FACE);
            var sketch = newSketch(context, id + "F34", { "sketchPlane" : qUnion([Q0])});
            skLineSegment(sketch, "E19", {"start": v(0, 0) * mm, "end": v(11.71, 23.13) * mm, "construction": true});
            skSolve(sketch);
        }
        {
            var Q0;
            Q0=sQuery(id+"F34.wireOp",EDGE,"E19");
            cPlane(context, id + "F35", {"entities" : qUnion([Q0]), "cplaneType" : CPlaneType.LINE_ANGLE, "offset" : 25 * mm, "angle" : 0 * degree, "width" : 150 * mm, "height" : 150 * mm});
        }
        {
            var Q0;
            Q0=qCreatedBy(id+"F35.planeOp",FACE);
            var sketch = newSketch(context, id + "F36", { "sketchPlane" : qUnion([Q0])});
            skCircle(sketch, "E20", {"center": v(-4.4, -6.39) * mm, "radius": 4 * mm});
            skSolve(sketch);
        }
        {
            var Q0;
            Q0 = qSketchRegion(id + "F36", true);
            extrude(context, id + "F37", {"entities" : qUnion([Q0]), "operationType" : NewBodyOperationType.REMOVE, "depth" : 25.5 * mm, "offsetDistance" : 25 * mm});
        }
        {
            var Q0;
            Q0=makeQuery(id+"F37.boolean.opBoolean","INTERSECT",EDGE,{"derivedFrom":[makeQuery(id+"F18.boolean.opBoolean","COPY",FACE,{"derivedFrom":makeQuery(id+"F18.opExtrude","SWEPT_FACE",FACE,{"disambiguationData":[OSD([sQuery(id+"F16.wireOp",EDGE,"E11")])]})}),makeQuery(id+"F37.opExtrude","SWEPT_FACE",FACE,{"disambiguationData":[OSD([sQuery(id+"F36.wireOp",EDGE,"E20")])]})]});
            var Q1;
            Q1=makeQuery(id+"F33.boolean.opBoolean","INTERSECT",EDGE,{"derivedFrom":[makeQuery(id+"F18.boolean.opBoolean","COPY",FACE,{"derivedFrom":makeQuery(id+"F18.opExtrude","SWEPT_FACE",FACE,{"disambiguationData":[OSD([sQuery(id+"F16.wireOp",EDGE,"E11")])]})}),makeQuery(id+"F33.opExtrude","SWEPT_FACE",FACE,{"disambiguationData":[OSD([sQuery(id+"F32.wireOp",EDGE,"E18")])]})]});
            fillet(context, id + "F38", {"entities" : qUnion([Q0, Q1]), "radius" : 5 * mm, "tangentPropagation" : true, "allowEdgeOverflow" : false});
        }
    });
